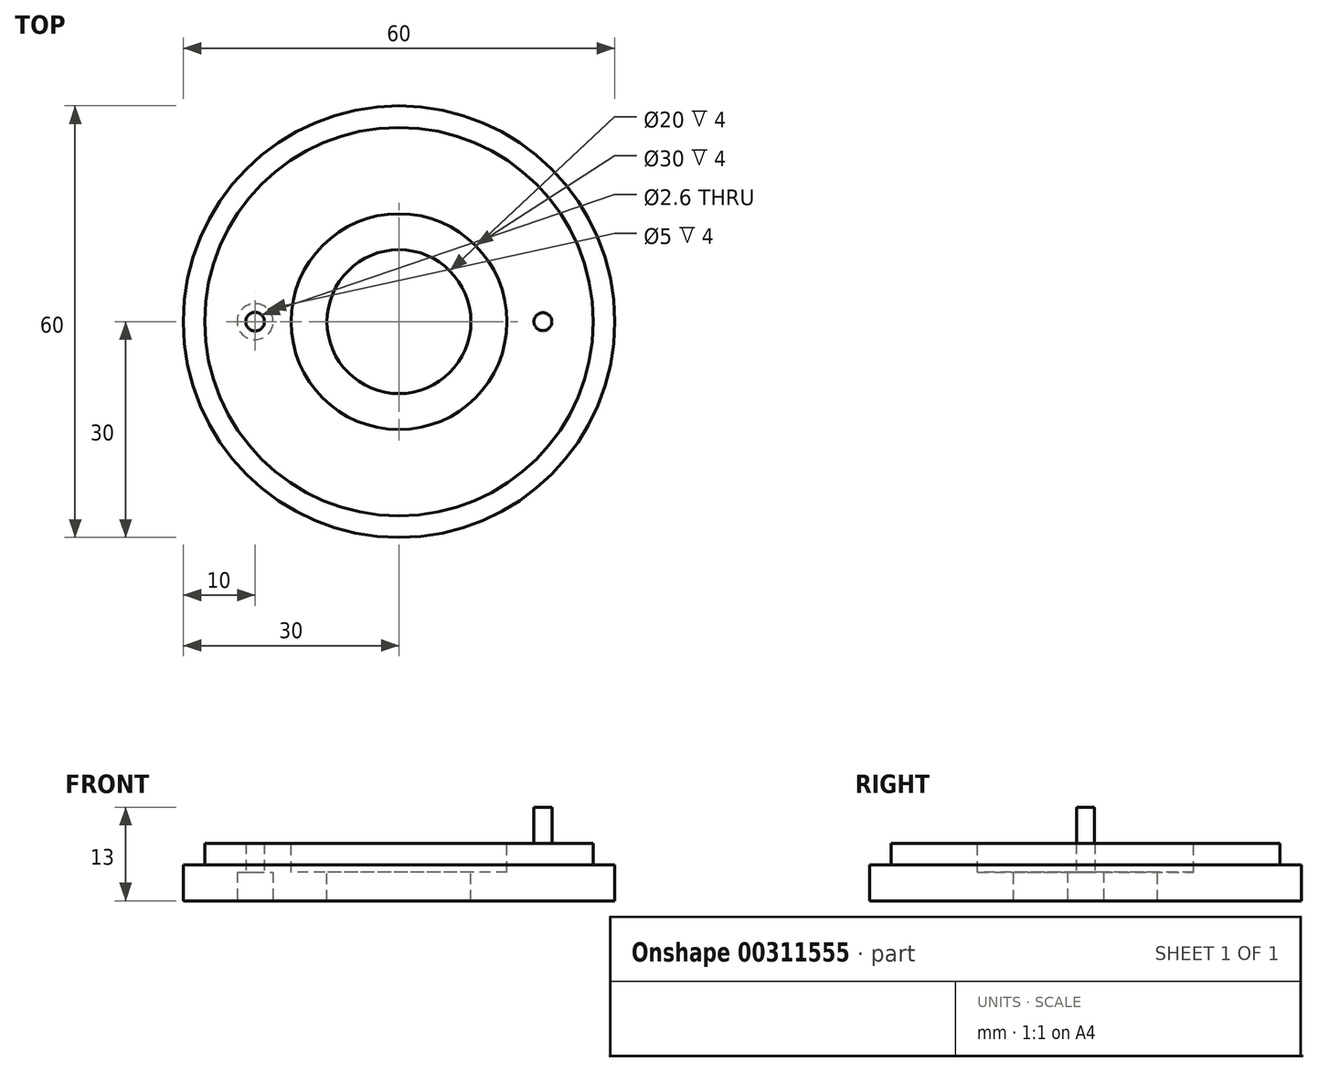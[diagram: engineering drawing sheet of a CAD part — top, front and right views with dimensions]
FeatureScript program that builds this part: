
annotation { "Feature Type Name" : "Feature", "Feature Type Description" : "" }
export const myFeature = defineFeature(function(context is Context, id is Id, definition is map)
    precondition{}
    {
        {
            var Q0;
            Q0=qCreatedBy(makeId("Front.planeOp"),FACE);
            var sketch = newSketch(context, id + "F0", { "sketchPlane" : qUnion([Q0])});
            skLineSegment(sketch, "E0", {"start": v(10, 0) * mm, "end": v(10, 4) * mm});
            skLineSegment(sketch, "E1", {"start": v(10, 4) * mm, "end": v(15, 4) * mm});
            skLineSegment(sketch, "E2", {"start": v(15, 4) * mm, "end": v(15, 8) * mm});
            skLineSegment(sketch, "E3", {"start": v(15, 8) * mm, "end": v(30, 8) * mm});
            skLineSegment(sketch, "E4", {"start": v(30, 8) * mm, "end": v(30, 0) * mm});
            skLineSegment(sketch, "E5", {"start": v(30, 0) * mm, "end": v(10, 0) * mm});
            skLineSegment(sketch, "E6", {"start": v(0, 45.72) * mm, "end": v(0, -41.8) * mm});
            skSolve(sketch);
        }
        {
            var Q0;
            Q0=makeQuery(id+"F0.imprint","IMPRINT",FACE,{"disambiguationData":[TD([[makeQuery(id+"F0.imprint","IMPRINT",EDGE,{"derivedFrom":sQuery(id+"F0.wireOp",EDGE,"E0")}),-1.0]])]});
            var Q1;
            Q1=sQuery(id+"F0.wireOp",EDGE,"E6");
            revolve(context, id + "F1", {"entities" : qUnion([Q0]), "axis" : qUnion([Q1]), "revolveType" : RevolveType.FULL});
        }
        {
            var Q0;
            Q0=makeQuery(id+"F1.opRevolve","SWEPT_FACE",FACE,{"disambiguationData":[OSD([sQuery(id+"F0.wireOp",EDGE,"E3")])]});
            var sketch = newSketch(context, id + "F2", { "sketchPlane" : qUnion([Q0])});
            skCircle(sketch, "E7", {"center": v(20, 0) * mm, "radius": 1.25 * mm});
            skSolve(sketch);
        }
        {
            var Q0;
            Q0 = qSketchRegion(id + "F2", true);
            extrude(context, id + "F3", {"entities" : qUnion([Q0]), "operationType" : NewBodyOperationType.ADD, "depth" : 5 * mm});
        }
        {
            var Q0;
            Q0=makeQuery(id+"F1.opRevolve","SWEPT_FACE",FACE,{"disambiguationData":[OSD([sQuery(id+"F0.wireOp",EDGE,"E5")])]});
            var sketch = newSketch(context, id + "F4", { "sketchPlane" : qUnion([Q0])});
            skPoint(sketch, "E8", {"position": v(-20, 0) * mm});
            skSolve(sketch);
        }
        {
            var Q0;
            Q0=sQuery(id+"F4.wireOp",VERTEX,"E8");
            var Q1;
            Q1=makeQuery(id+"F1.opRevolve","SWEPT_BODY",BODY,{"disambiguationData":[OSD([sQuery(id+"F0.wireOp",EDGE,"E0"),sQuery(id+"F0.wireOp",EDGE,"E1"),sQuery(id+"F0.wireOp",EDGE,"E2"),sQuery(id+"F0.wireOp",EDGE,"E3"),sQuery(id+"F0.wireOp",EDGE,"E4"),sQuery(id+"F0.wireOp",EDGE,"E5")])]});
            hole(context, id + "F5", {"style" : HoleStyle.C_BORE, "endStyle" : HoleEndStyle.THROUGH, "holeDiameter" : 2.6 * mm, "cBoreDiameter" : 5 * mm, "cBoreDepth" : 4 * mm, "tappedDepth" : 12 * mm, "tapClearance" : 3, "startFromSketch" : true, "locations" : qUnion([Q0]), "scope" : qUnion([Q1])});
        }
        {
            var Q0;
            Q0=qCreatedBy(makeId("Front.planeOp"),FACE);
            var sketch = newSketch(context, id + "F6", { "sketchPlane" : qUnion([Q0])});
            skLineSegment(sketch, "E9.bottom", {"start": v(30, 8) * mm, "end": v(27, 8) * mm});
            skLineSegment(sketch, "E9.top", {"start": v(30, 5) * mm, "end": v(27, 5) * mm});
            skLineSegment(sketch, "E9.left", {"start": v(30, 8) * mm, "end": v(30, 5) * mm});
            skLineSegment(sketch, "E9.right", {"start": v(27, 8) * mm, "end": v(27, 5) * mm});
            skSolve(sketch);
        }
        {
            var Q0;
            Q0 = qSketchRegion(id + "F6", true);
            var Q1;
            Q1=sQuery(id+"F0.wireOp",EDGE,"E6");
            revolve(context, id + "F7", {"operationType" : NewBodyOperationType.REMOVE, "entities" : qUnion([Q0]), "axis" : qUnion([Q1]), "revolveType" : RevolveType.FULL, "oppositeDirection" : true});
        }
    });
